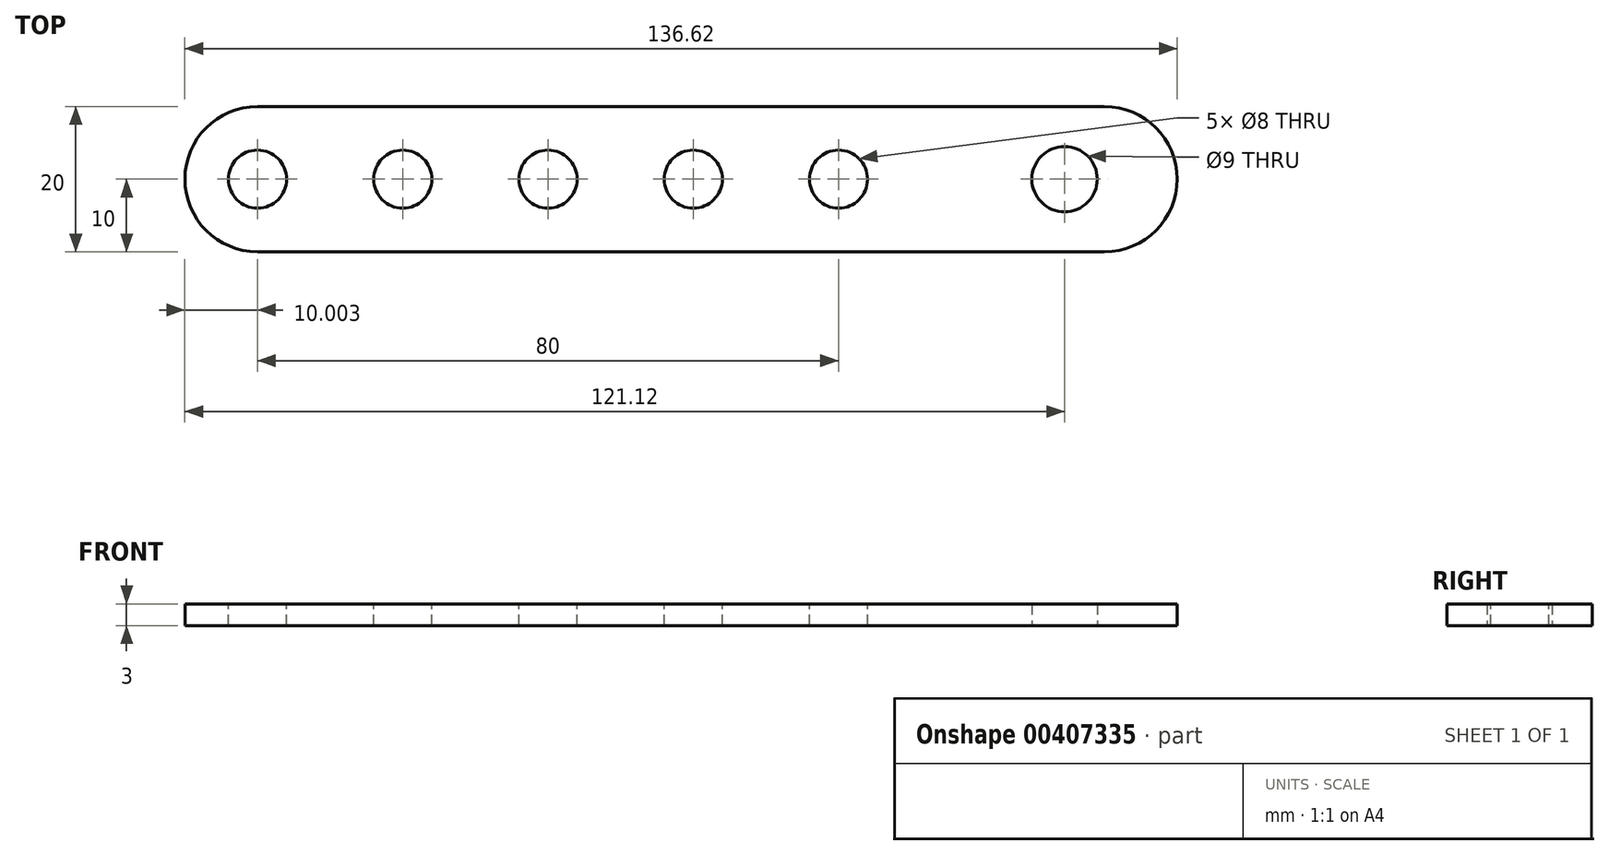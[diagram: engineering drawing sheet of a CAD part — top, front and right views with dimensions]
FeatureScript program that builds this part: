
annotation { "Feature Type Name" : "Feature", "Feature Type Description" : "" }
export const myFeature = defineFeature(function(context is Context, id is Id, definition is map)
    precondition{}
    {
        {
            var Q0;
            Q0=qCreatedBy(makeId("Top.planeOp"),FACE);
            var sketch = newSketch(context, id + "F0", { "sketchPlane" : qUnion([Q0])});
            skLineSegment(sketch, "E0.bottom", {"start": v(5.5, 10) * mm, "end": v(-111.12, 10) * mm});
            skLineSegment(sketch, "E0.top", {"start": v(5.5, -10) * mm, "end": v(-111.12, -10) * mm});
            skArc(sketch, "E1", {"start": v(-111.12, 10) * mm, "mid": v(-121.12, 0) * mm, "end": v(-111.12, -10) * mm});
            skArc(sketch, "E2", {"start": v(5.5, -10) * mm, "mid": v(15.5, 0) * mm, "end": v(5.5, 10) * mm});
            skCircle(sketch, "E3", {"center": v(0, 0) * mm, "radius": 4.5 * mm});
            skSolve(sketch);
        }
        {
            var Q0;
            Q0=makeQuery(id+"F0.imprint","IMPRINT",FACE,{"disambiguationData":[TD([[makeQuery(id+"F0.imprint","IMPRINT",EDGE,{"derivedFrom":sQuery(id+"F0.wireOp",EDGE,"E0.bottom")}),1.0]])]});
            extrude(context, id + "F1", {"entities" : qUnion([Q0]), "depth" : 3 * mm});
        }
        {
            var Q0;
            Q0=makeQuery(id+"F1.opExtrude","CAP_FACE",FACE,{"disambiguationData":[OSD([sQuery(id+"F0.wireOp",EDGE,"E0.bottom"),sQuery(id+"F0.wireOp",EDGE,"E0.top"),sQuery(id+"F0.wireOp",EDGE,"E1"),sQuery(id+"F0.wireOp",EDGE,"E2"),sQuery(id+"F0.wireOp",EDGE,"E3")])],"isStart":false});
            var sketch = newSketch(context, id + "F2", { "sketchPlane" : qUnion([Q0])});
            skCircle(sketch, "E4", {"center": v(-111.12, 0) * mm, "radius": 4 * mm});
            skCircle(sketch, "E5.1.0.0", {"center": v(-91.12, 0) * mm, "radius": 4 * mm});
            skCircle(sketch, "E5.2.0.0", {"center": v(-71.12, 0) * mm, "radius": 4 * mm});
            skCircle(sketch, "E5.3.0.0", {"center": v(-51.12, 0) * mm, "radius": 4 * mm});
            skCircle(sketch, "E5.4.0.0", {"center": v(-31.12, 0) * mm, "radius": 4 * mm});
            skLineSegment(sketch, "E5.direction1", {"start": v(-111.12, 0) * mm, "end": v(-91.12, 0) * mm, "construction": true});
            skSolve(sketch);
        }
        {
            var Q0;
            Q0=makeQuery(id+"F2.imprint","IMPRINT",FACE,{"disambiguationData":[TD([[makeQuery(id+"F2.imprint","IMPRINT",EDGE,{"derivedFrom":sQuery(id+"F2.wireOp",EDGE,"E4")}),1.0]])]});
            var Q1;
            Q1=makeQuery(id+"F2.imprint","IMPRINT",FACE,{"disambiguationData":[TD([[makeQuery(id+"F2.imprint","IMPRINT",EDGE,{"derivedFrom":sQuery(id+"F2.wireOp",EDGE,"E5.1.0.0")}),1.0]])]});
            var Q2;
            Q2=makeQuery(id+"F2.imprint","IMPRINT",FACE,{"disambiguationData":[TD([[makeQuery(id+"F2.imprint","IMPRINT",EDGE,{"derivedFrom":sQuery(id+"F2.wireOp",EDGE,"E5.2.0.0")}),1.0]])]});
            var Q3;
            Q3=makeQuery(id+"F2.imprint","IMPRINT",FACE,{"disambiguationData":[TD([[makeQuery(id+"F2.imprint","IMPRINT",EDGE,{"derivedFrom":sQuery(id+"F2.wireOp",EDGE,"E5.3.0.0")}),1.0]])]});
            var Q4;
            Q4=makeQuery(id+"F2.imprint","IMPRINT",FACE,{"disambiguationData":[TD([[makeQuery(id+"F2.imprint","IMPRINT",EDGE,{"derivedFrom":sQuery(id+"F2.wireOp",EDGE,"E5.4.0.0")}),1.0]])]});
            extrude(context, id + "F3", {"entities" : qUnion([Q0, Q1, Q2, Q3, Q4]), "operationType" : NewBodyOperationType.REMOVE, "endBound" : BoundingType.THROUGH_ALL, "oppositeDirection" : true, "depth" : 25 * mm});
        }
    });
